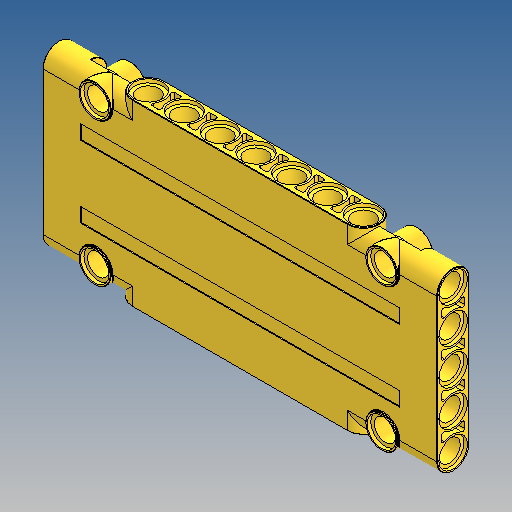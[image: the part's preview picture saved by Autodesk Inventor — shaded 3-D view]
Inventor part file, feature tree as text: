
AUTODESK INVENTOR PART (.ipt)
format: ipt  version: 2025 (Build 290162010, 162A)  size: 1,130,496 bytes
history: native  units: in
note: dims shown in document units (in); Inventor stores cm internally (conversion verified against a paired STEP export)
features: extrude x16, sketch x11, mirror x3, plane x1, fillet x1
ambient origin geometry x8: Origin, YZ Plane, XZ Plane, XY Plane, X Axis, Y Axis, Z Axis, Center Point
bodies: Solid1 (feature_tree)
feature tree (32):
  extrude  "Extrusion1"  Depth=0.189in
  sketch  "Sketch3"  dims[d6=0.189in d7=0.252in]
  extrude  "Extrusion2"  Depth=0.0315in
  extrude  "Extrusion3"  TaperAngle=0.0deg  [1 undecoded]
  extrude  "Extrusion4"  Depth=0.252in
  plane  "Work Plane1"
  extrude  "Extrusion5"  Depth=1.5748in
  sketch  "Sketch5"  dims[d12=0.3937in d14=0.3937in d16=0.2835in]
  extrude  "Extrusion6"  Depth=0.2835in
  extrude  "Extrusion7"  Depth=0.0315in
  extrude  "Extrusion10"  Depth=0.2205in TaperAngle=0.0deg
  extrude  "Extrusion8"  Depth=0.189in
  extrude  "Extrusion9"  Depth=0.0315in TaperAngle=0.0deg
  mirror  "Mirror1"
  mirror  "Mirror2"
  sketch  "Sketch8"  dims[d22=-0.1417in d23=0.189in]
  extrude  "Extrusion11"  Depth=0.189in
  extrude  "Extrusion12"  Depth=0.0157in
  extrude  "Extrusion13"  Depth=0.0472in
  sketch  "Sketch9"  dims[d24=0.2835in d25=0.0315in d26=0.0in]
  extrude  "Extrusion14"  TaperAngle=0.0deg  [1 undecoded]
  extrude  "Extrusion16"  Depth=0.0157in TaperAngle=0.0deg
  mirror  "Mirror3"
  extrude  "Extrusion15"  Depth=0.252in
  fillet  "Fillet1"  Radius=0.0315in
  sketch  "Sketch2"  dims[d2=0.2835in d3=0.0315in]
  sketch  "Skizze - Rechteckige Anordnung1"  dims[d0=0.315in d1=0.189in]
  sketch  "Sketch4"  dims[d8=45.0deg d9=1.5748in d11=0.315in]
  sketch  "Sketch6"  dims[d17=0.0in d18=0.0315in]
  sketch  "Sketch7"  dims[d19=0.0in d20=0.2205in d21=0.0in]
  sketch  "Sketch10"  dims[d27=0.2835in d28=0.189in d29=1.2598in d30=0.2677in d31=0.0472in d32=0.0in d33=0.0in d34=0.2677in d35=0.0in d36=0.252in d37=0.0315in d38=0.0in d39=0.252in d40=0.0315in d41=0.0in d42=0.0315in d43=0.2205in d44=0.0in d45=0.2835in d46=1.8898in d47=0.189in d48=0.1417in d49=0.1417in d50=0.0in d51=0.0in d52=0.1417in d53=0.0in d54=0.315in d55=0.0in d56=0.252in d57=0.0315in d58=0.0in d59=2.8031in d60=0.126in d61=0.5039in d62=0.0079in d63=0.0in d64=45.0deg d65=2.3622in d67=0.315in d68=0.3937in d70=0.3937in d72=0.2205in d73=0.0in d74=0.0039in d75=0.0157in]
  sketch  "Skizze - Rechteckige Anordnung2"  dims[d4=3.4646in d5=0.0in]
note: 2 required parameter values undecoded (feature->parameter linkage not recoverable at this tier; creation-order binding heuristic only, values carry confidence <= 0.55)
